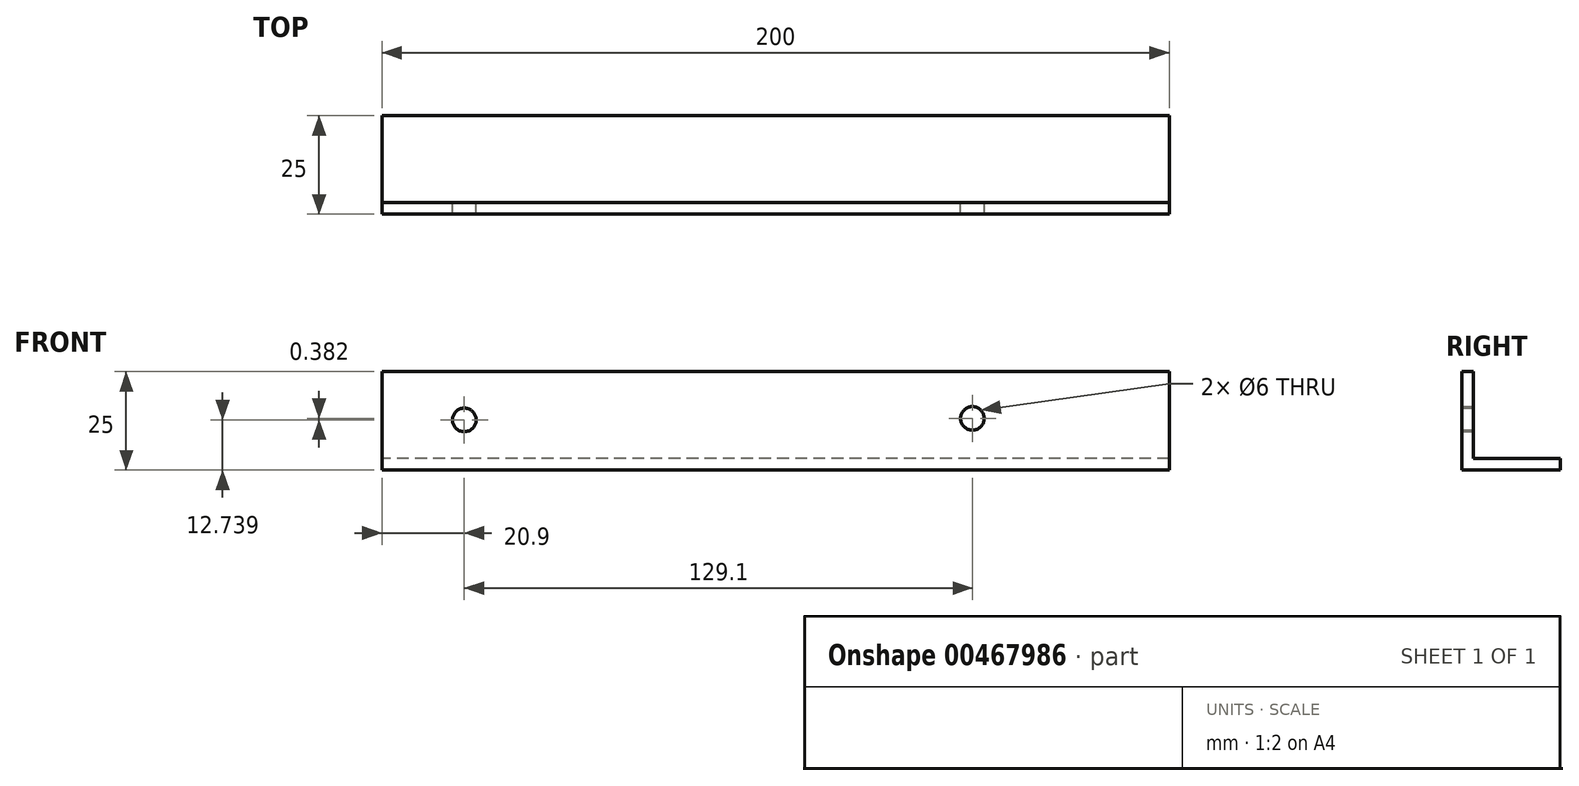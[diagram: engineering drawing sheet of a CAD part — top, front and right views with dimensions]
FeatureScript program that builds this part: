
annotation { "Feature Type Name" : "Feature", "Feature Type Description" : "" }
export const myFeature = defineFeature(function(context is Context, id is Id, definition is map)
    precondition{}
    {
        {
            var Q0;
            Q0=qCreatedBy(makeId("Right.planeOp"),FACE);
            var sketch = newSketch(context, id + "F0", { "sketchPlane" : qUnion([Q0])});
            skLineSegment(sketch, "E0", {"start": v(0, 25) * mm, "end": v(0, 0) * mm});
            skLineSegment(sketch, "E1", {"start": v(0, 0) * mm, "end": v(25, 0) * mm});
            skLineSegment(sketch, "E2", {"start": v(25, 0) * mm, "end": v(25, 3) * mm});
            skLineSegment(sketch, "E3", {"start": v(25, 3) * mm, "end": v(3, 3) * mm});
            skLineSegment(sketch, "E4", {"start": v(3, 3) * mm, "end": v(3, 25) * mm});
            skLineSegment(sketch, "E5", {"start": v(3, 25) * mm, "end": v(0, 25) * mm});
            skSolve(sketch);
        }
        {
            var Q0;
            Q0 = qSketchRegion(id + "F0", true);
            extrude(context, id + "F1", {"entities" : qUnion([Q0]), "depth" : 200 * mm});
        }
        {
            var Q0;
            Q0=makeQuery(id+"F1.opExtrude","SWEPT_FACE",FACE,{"disambiguationData":[OSD([sQuery(id+"F0.wireOp",EDGE,"E4")])]});
            var sketch = newSketch(context, id + "F2", { "sketchPlane" : qUnion([Q0])});
            skCircle(sketch, "E6", {"center": v(-150, 13.12) * mm, "radius": 3 * mm});
            skCircle(sketch, "E7", {"center": v(-20.9, 12.74) * mm, "radius": 3 * mm});
            skSolve(sketch);
        }
        {
            var Q0;
            Q0 = qSketchRegion(id + "F2", true);
            extrude(context, id + "F3", {"entities" : qUnion([Q0]), "operationType" : NewBodyOperationType.REMOVE, "oppositeDirection" : true, "depth" : 25 * mm});
        }
    });
